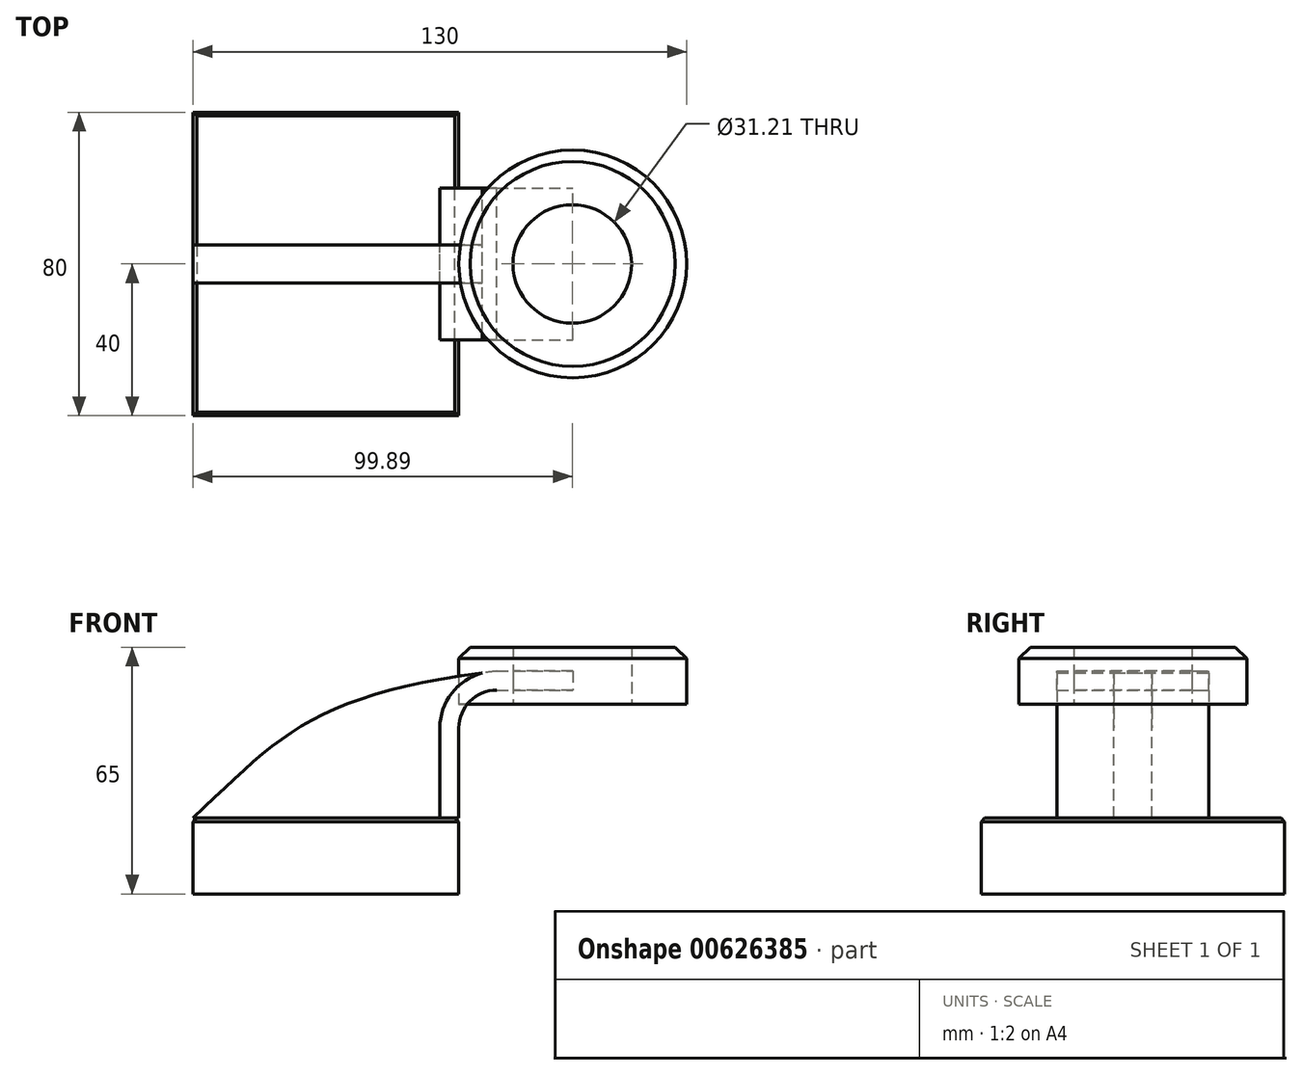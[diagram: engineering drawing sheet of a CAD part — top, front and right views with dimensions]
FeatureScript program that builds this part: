
annotation { "Feature Type Name" : "Feature", "Feature Type Description" : "" }
export const myFeature = defineFeature(function(context is Context, id is Id, definition is map)
    precondition{}
    {
        {
            var Q0;
            Q0=qCreatedBy(makeId("Front.planeOp"),FACE);
            var sketch = newSketch(context, id + "F0", { "sketchPlane" : qUnion([Q0])});
            skLineSegment(sketch, "E0.bottom", {"start": v(35, -10) * mm, "end": v(-35, -10) * mm});
            skLineSegment(sketch, "E0.top", {"start": v(35, 10) * mm, "end": v(-35, 10) * mm});
            skLineSegment(sketch, "E0.left", {"start": v(35, -10) * mm, "end": v(35, 10) * mm});
            skLineSegment(sketch, "E0.right", {"start": v(-35, -10) * mm, "end": v(-35, 10) * mm});
            skPoint(sketch, "E0.middle", {"position": v(0, 0) * mm});
            skLineSegment(sketch, "E1.bottom", {"start": v(95, 40) * mm, "end": v(55, 40) * mm});
            skLineSegment(sketch, "E1.top", {"start": v(95, 55) * mm, "end": v(55, 55) * mm});
            skLineSegment(sketch, "E1.left", {"start": v(95, 40) * mm, "end": v(95, 55) * mm});
            skLineSegment(sketch, "E1.right", {"start": v(55, 40) * mm, "end": v(55, 55) * mm});
            skPoint(sketch, "E1.middle", {"position": v(75, 47.5) * mm});
            skLineSegment(sketch, "E2", {"start": v(35, 10) * mm, "end": v(35, 33.7) * mm});
            skArc(sketch, "E3", {"start": v(35, 33.7) * mm, "mid": v(37.93, 40.77) * mm, "end": v(45, 43.7) * mm});
            skLineSegment(sketch, "E4", {"start": v(45, 43.7) * mm, "end": v(65, 43.7) * mm});
            skLineSegment(sketch, "E5.0", {"start": v(45, 48.7) * mm, "end": v(65, 48.7) * mm});
            skArc(sketch, "E5.1", {"start": v(30, 33.7) * mm, "mid": v(34.4, 44.3) * mm, "end": v(45, 48.7) * mm});
            skLineSegment(sketch, "E5.2", {"start": v(30, 10) * mm, "end": v(30, 33.7) * mm});
            skLineSegment(sketch, "E6", {"start": v(65, 40) * mm, "end": v(65, 55) * mm});
            skFitSpline(sketch, "E7", {"points": [v(-35, 10) * mm, v(45, 48.7) * mm], "startDerivative": vector(70.2, 66.93) * mm, "endDerivative": vector(143.8, 17.6) * mm});
            skSolve(sketch);
        }
        {
            var Q0;
            Q0=makeQuery(id+"F0.imprint","IMPRINT",FACE,{"disambiguationData":[TD([[makeQuery(id+"F0.imprint","IMPRINT",EDGE,{"derivedFrom":sQuery(id+"F0.wireOp",EDGE,"E0.bottom")}),-1.0]])]});
            extrude(context, id + "F1", {"entities" : qUnion([Q0]), "endBound" : BoundingType.SYMMETRIC, "depth" : 80 * mm, "offsetDistance" : 25 * mm});
        }
        {
            var Q0;
            {var subQ1=sQuery(id+"F0.wireOp",EDGE,"E2");Q0=makeQuery(id+"F0.imprint","IMPRINT",FACE,{"disambiguationData":[TD([[makeQuery(id+"F0.imprint","IMPRINT",EDGE,{"derivedFrom":subQ1}),1.0]])]});}
            var Q1;
            {var subQ0=sQuery(id+"F0.wireOp",EDGE,"E4");var subQ1=sQuery(id+"F0.wireOp",EDGE,"E1.right");var subQ2=makeQuery(id+"F0.imprint","INTERSECT",VERTEX,{"derivedFrom":[subQ1,subQ0]});Q1=makeQuery(id+"F0.imprint","IMPRINT",FACE,{"disambiguationData":[TD([[makeQuery(id+"F0.imprint","IMPRINT",EDGE,{"disambiguationData":[TD([[subQ2,-1.0]])],"derivedFrom":subQ1}),-1.0]])]});}
            extrude(context, id + "F2", {"entities" : qUnion([Q0, Q1]), "endBound" : BoundingType.SYMMETRIC, "depth" : 40 * mm, "offsetDistance" : 25 * mm});
        }
        {
            var Q0;
            {var subQ3=sQuery(id+"F0.wireOp",EDGE,"E5.2");Q0=makeQuery(id+"F0.imprint","IMPRINT",FACE,{"disambiguationData":[TD([[makeQuery(id+"F0.imprint","IMPRINT",EDGE,{"derivedFrom":subQ3}),1.0]])]});}
            extrude(context, id + "F3", {"entities" : qUnion([Q0]), "endBound" : BoundingType.SYMMETRIC, "depth" : 10 * mm, "offsetDistance" : 25 * mm});
        }
        {
            var Q0;
            {var subQ0=sQuery(id+"F0.wireOp",EDGE,"E1.left");Q0=makeQuery(id+"F0.imprint","IMPRINT",FACE,{"disambiguationData":[TD([[makeQuery(id+"F0.imprint","IMPRINT",EDGE,{"derivedFrom":subQ0}),1.0]])]});}
            var Q1;
            Q1=sQuery(id+"F0.wireOp",EDGE,"E6");
            revolve(context, id + "F4", {"entities" : qUnion([Q0]), "axis" : qUnion([Q1]), "revolveType" : RevolveType.FULL});
        }
        {
            var Q0;
            Q0=makeQuery(id+"F1.opExtrude","SWEPT_FACE",FACE,{"disambiguationData":[OSD([sQuery(id+"F0.wireOp",EDGE,"E0.top")])]});
            chamfer(context, id + "F5", {"entities" : qUnion([Q0]), "width" : 1 * mm, "tangentPropagation" : true});
        }
        {
            var Q0;
            Q0=makeQuery(id+"F4.opRevolve","SWEPT_EDGE",EDGE,{"disambiguationData":[OSD([sQuery(id+"F0.wireOp",EDGE,"E1.top"),sQuery(id+"F0.wireOp",EDGE,"E1.left")])]});
            chamfer(context, id + "F6", {"entities" : qUnion([Q0]), "width" : 3 * mm, "tangentPropagation" : true});
        }
        {
            var Q0;
            Q0=qCreatedBy(makeId("Top.planeOp"),FACE);
            var sketch = newSketch(context, id + "F7", { "sketchPlane" : qUnion([Q0])});
            skCircle(sketch, "E8", {"center": v(64.9, 0) * mm, "radius": 15.6 * mm});
            skSolve(sketch);
        }
        {
            var Q0;
            Q0=makeQuery(id+"F7.imprint","IMPRINT",FACE,{"disambiguationData":[TD([[makeQuery(id+"F7.imprint","IMPRINT",EDGE,{"derivedFrom":sQuery(id+"F7.wireOp",EDGE,"E8")}),1.0]])]});
            extrude(context, id + "F8", {"entities" : qUnion([Q0]), "operationType" : NewBodyOperationType.REMOVE, "depth" : 82.8 * mm, "offsetDistance" : 25 * mm});
        }
    });
